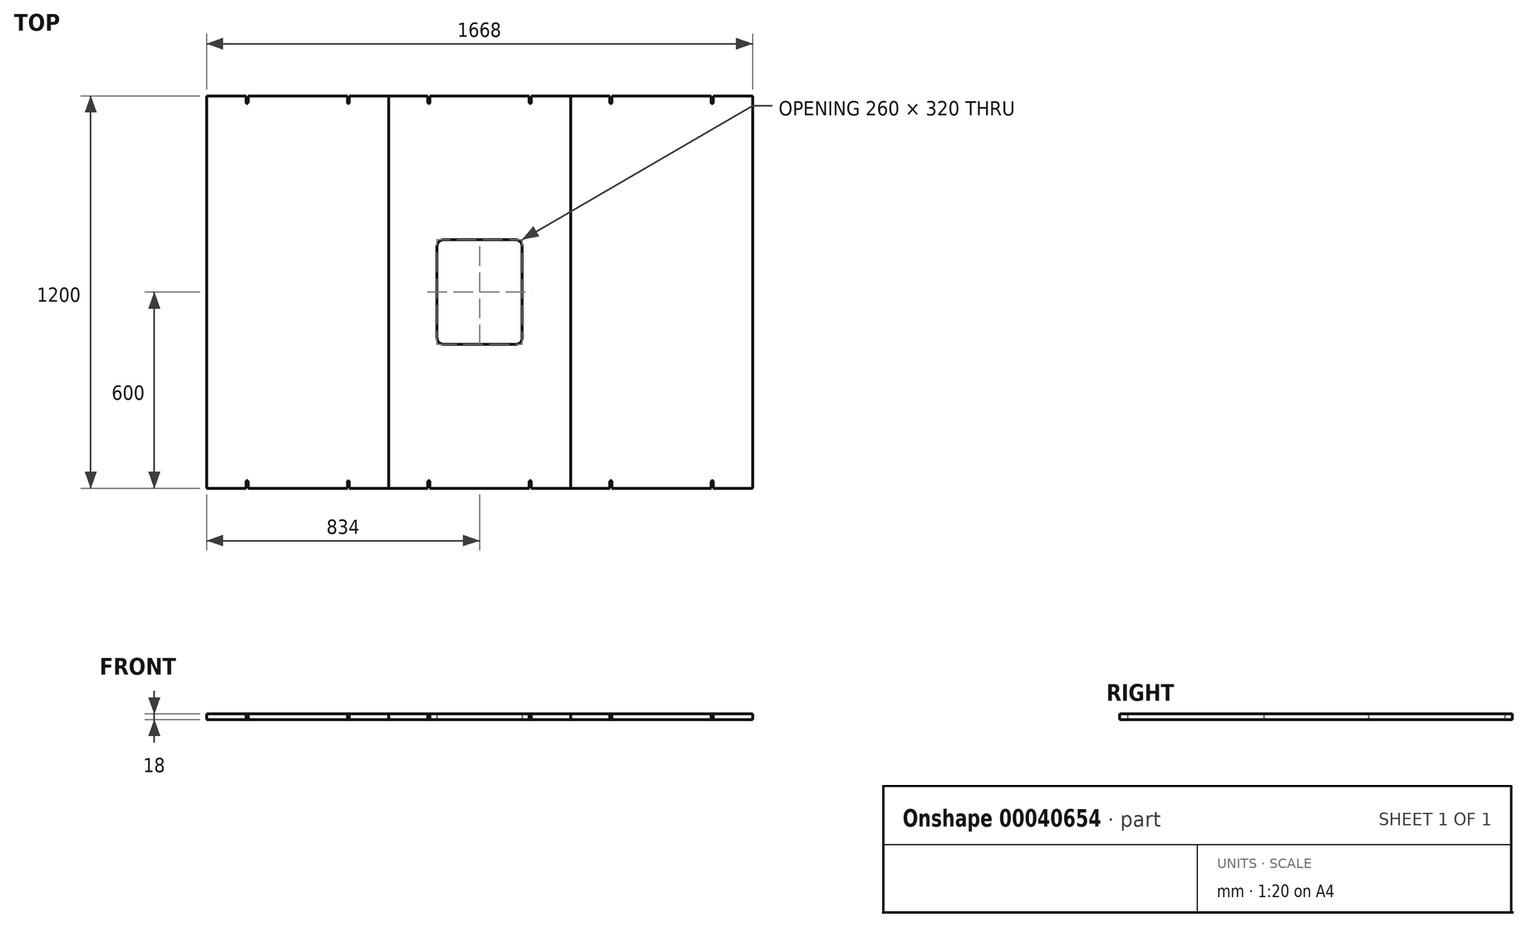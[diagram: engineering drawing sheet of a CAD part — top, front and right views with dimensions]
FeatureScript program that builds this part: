
annotation { "Feature Type Name" : "Feature", "Feature Type Description" : "" }
export const myFeature = defineFeature(function(context is Context, id is Id, definition is map)
    precondition{}
    {
        {
            var Q0;
            Q0=qCreatedBy(makeId("Top.planeOp"),FACE);
            var sketch = newSketch(context, id + "F0", { "sketchPlane" : qUnion([Q0])});
            skLineSegment(sketch, "E0.left", {"start": v(834, 600) * mm, "end": v(834, -600) * mm});
            skLineSegment(sketch, "E0.right", {"start": v(-834, 600) * mm, "end": v(-834, -600) * mm});
            skPoint(sketch, "E0.middle", {"position": v(0, 0) * mm});
            skLineSegment(sketch, "E1.bottom", {"start": v(130, 160) * mm, "end": v(-130, 160) * mm});
            skLineSegment(sketch, "E1.top", {"start": v(130, -160) * mm, "end": v(-130, -160) * mm});
            skLineSegment(sketch, "E1.left", {"start": v(130, 160) * mm, "end": v(130, -160) * mm});
            skLineSegment(sketch, "E1.right", {"start": v(-130, 160) * mm, "end": v(-130, -160) * mm});
            skLineSegment(sketch, "E2", {"start": v(-278, 600) * mm, "end": v(-278, -600) * mm});
            skLineSegment(sketch, "E3", {"start": v(278, 600) * mm, "end": v(278, -600) * mm});
            skLineSegment(sketch, "E4", {"start": v(-834, 600) * mm, "end": v(-278, 600) * mm});
            skLineSegment(sketch, "E5", {"start": v(-278, 600) * mm, "end": v(278, 600) * mm});
            skLineSegment(sketch, "E6", {"start": v(278, 600) * mm, "end": v(834, 600) * mm});
            skLineSegment(sketch, "E7", {"start": v(-834, -600) * mm, "end": v(-278, -600) * mm});
            skLineSegment(sketch, "E8", {"start": v(-278, -600) * mm, "end": v(278, -600) * mm});
            skLineSegment(sketch, "E9", {"start": v(278, -600) * mm, "end": v(834, -600) * mm});
            skArc(sketch, "E10", {"start": v(-714, 580) * mm, "mid": v(-710.9, 576.9) * mm, "end": v(-707.8, 580) * mm});
            skLineSegment(sketch, "E11.top", {"start": v(-714, 600) * mm, "end": v(-707.8, 600) * mm});
            skLineSegment(sketch, "E11.left", {"start": v(-714, 580) * mm, "end": v(-714, 600) * mm});
            skLineSegment(sketch, "E11.right", {"start": v(-707.8, 580) * mm, "end": v(-707.8, 600) * mm});
            skLineSegment(sketch, "E12", {"start": v(-556, 600) * mm, "end": v(-556, 638.6) * mm, "construction": true});
            skLineSegment(sketch, "E13.MirrorCS", {"start": v(-404.2, 580) * mm, "end": v(-404.2, 600) * mm});
            skArc(sketch, "E14.MirrorCS", {"start": v(-398, 580) * mm, "mid": v(-401.1, 576.9) * mm, "end": v(-404.2, 580) * mm});
            skLineSegment(sketch, "E15.MirrorCS", {"start": v(-398, 580) * mm, "end": v(-398, 600) * mm});
            skLineSegment(sketch, "E16.1.0.0", {"start": v(-158, 580) * mm, "end": v(-158, 600) * mm});
            skArc(sketch, "E16.1.0.1", {"start": v(-158, 580) * mm, "mid": v(-154.9, 576.9) * mm, "end": v(-151.8, 580) * mm});
            skLineSegment(sketch, "E16.1.0.2", {"start": v(-151.8, 580) * mm, "end": v(-151.8, 600) * mm});
            skLineSegment(sketch, "E16.1.0.3", {"start": v(151.8, 580) * mm, "end": v(151.8, 600) * mm});
            skArc(sketch, "E16.1.0.4", {"start": v(158, 580) * mm, "mid": v(154.9, 576.9) * mm, "end": v(151.8, 580) * mm});
            skLineSegment(sketch, "E16.1.0.5", {"start": v(158, 580) * mm, "end": v(158, 600) * mm});
            skLineSegment(sketch, "E16.2.0.0", {"start": v(398, 580) * mm, "end": v(398, 600) * mm});
            skArc(sketch, "E16.2.0.1", {"start": v(398, 580) * mm, "mid": v(401.1, 576.9) * mm, "end": v(404.2, 580) * mm});
            skLineSegment(sketch, "E16.2.0.2", {"start": v(404.2, 580) * mm, "end": v(404.2, 600) * mm});
            skLineSegment(sketch, "E16.2.0.3", {"start": v(707.8, 580) * mm, "end": v(707.8, 600) * mm});
            skArc(sketch, "E16.2.0.4", {"start": v(714, 580) * mm, "mid": v(710.9, 576.9) * mm, "end": v(707.8, 580) * mm});
            skLineSegment(sketch, "E16.2.0.5", {"start": v(714, 580) * mm, "end": v(714, 600) * mm});
            skLineSegment(sketch, "E16.direction1", {"start": v(-714, 580) * mm, "end": v(-158, 580) * mm, "construction": true});
            skLineSegment(sketch, "E17.MirrorCS", {"start": v(-714, -580) * mm, "end": v(-714, -600) * mm});
            skArc(sketch, "E18.MirrorCS", {"start": v(-714, -580) * mm, "mid": v(-710.9, -576.9) * mm, "end": v(-707.8, -580) * mm});
            skLineSegment(sketch, "E19.MirrorCS", {"start": v(-707.8, -580) * mm, "end": v(-707.8, -600) * mm});
            skLineSegment(sketch, "E20.MirrorCS", {"start": v(-404.2, -580) * mm, "end": v(-404.2, -600) * mm});
            skArc(sketch, "E21.MirrorCS", {"start": v(-398, -580) * mm, "mid": v(-401.1, -576.9) * mm, "end": v(-404.2, -580) * mm});
            skLineSegment(sketch, "E22.MirrorCS", {"start": v(-398, -580) * mm, "end": v(-398, -600) * mm});
            skLineSegment(sketch, "E23.MirrorCS", {"start": v(-158, -580) * mm, "end": v(-158, -600) * mm});
            skArc(sketch, "E24.MirrorCS", {"start": v(-158, -580) * mm, "mid": v(-154.9, -576.9) * mm, "end": v(-151.8, -580) * mm});
            skLineSegment(sketch, "E25.MirrorCS", {"start": v(-151.8, -580) * mm, "end": v(-151.8, -600) * mm});
            skLineSegment(sketch, "E26.MirrorCS", {"start": v(151.8, -580) * mm, "end": v(151.8, -600) * mm});
            skArc(sketch, "E27.MirrorCS", {"start": v(158, -580) * mm, "mid": v(154.9, -576.9) * mm, "end": v(151.8, -580) * mm});
            skLineSegment(sketch, "E28.MirrorCS", {"start": v(158, -580) * mm, "end": v(158, -600) * mm});
            skLineSegment(sketch, "E29.MirrorCS", {"start": v(398, -580) * mm, "end": v(398, -600) * mm});
            skArc(sketch, "E30.MirrorCS", {"start": v(398, -580) * mm, "mid": v(401.1, -576.9) * mm, "end": v(404.2, -580) * mm});
            skLineSegment(sketch, "E31.MirrorCS", {"start": v(404.2, -580) * mm, "end": v(404.2, -600) * mm});
            skLineSegment(sketch, "E32.MirrorCS", {"start": v(707.8, -580) * mm, "end": v(707.8, -600) * mm});
            skArc(sketch, "E33.MirrorCS", {"start": v(714, -580) * mm, "mid": v(710.9, -576.9) * mm, "end": v(707.8, -580) * mm});
            skLineSegment(sketch, "E34.MirrorCS", {"start": v(714, -580) * mm, "end": v(714, -600) * mm});
            skSolve(sketch);
        }
        {
            var Q0;
            Q0=makeQuery(id+"F0.imprint","IMPRINT",FACE,{"disambiguationData":[TD([[makeQuery(id+"F0.imprint","IMPRINT",EDGE,{"derivedFrom":sQuery(id+"F0.wireOp",EDGE,"E1.bottom")}),-1.0]])]});
            extrude(context, id + "F1", {"entities" : qUnion([Q0]), "flatOperationType" : FlatOperationType.REMOVE, "depth" : 18 * mm, "offsetDistance" : 25 * mm, "domain" : OperationDomain.MODEL});
        }
        {
            var Q0;
            {var subQ5=sQuery(id+"F0.wireOp",EDGE,"E0.right");Q0=makeQuery(id+"F0.imprint","IMPRINT",FACE,{"disambiguationData":[TD([[makeQuery(id+"F0.imprint","IMPRINT",EDGE,{"derivedFrom":subQ5}),1.0]])]});}
            var Q1;
            Q1=makeQuery(id+"F1.opExtrude","CAP_FACE",FACE,{"disambiguationData":[OSD([sQuery(id+"F0.wireOp",EDGE,"E1.bottom"),sQuery(id+"F0.wireOp",EDGE,"E1.top"),sQuery(id+"F0.wireOp",EDGE,"E1.left"),sQuery(id+"F0.wireOp",EDGE,"E1.right"),sQuery(id+"F0.wireOp",EDGE,"E2"),sQuery(id+"F0.wireOp",EDGE,"E3"),sQuery(id+"F0.wireOp",EDGE,"E5"),sQuery(id+"F0.wireOp",EDGE,"E8"),sQuery(id+"F0.wireOp",EDGE,"E16.1.0.0"),sQuery(id+"F0.wireOp",EDGE,"E16.1.0.1"),sQuery(id+"F0.wireOp",EDGE,"E16.1.0.2"),sQuery(id+"F0.wireOp",EDGE,"E16.1.0.3"),sQuery(id+"F0.wireOp",EDGE,"E16.1.0.4"),sQuery(id+"F0.wireOp",EDGE,"E16.1.0.5"),sQuery(id+"F0.wireOp",EDGE,"E23.MirrorCS"),sQuery(id+"F0.wireOp",EDGE,"E24.MirrorCS"),sQuery(id+"F0.wireOp",EDGE,"E25.MirrorCS"),sQuery(id+"F0.wireOp",EDGE,"E26.MirrorCS"),sQuery(id+"F0.wireOp",EDGE,"E27.MirrorCS"),sQuery(id+"F0.wireOp",EDGE,"E28.MirrorCS")])],"isStart":false});
            extrude(context, id + "F2", {"entities" : qUnion([Q0]), "endBound" : BoundingType.UP_TO_SURFACE, "depth" : 18 * mm, "endBoundEntityFace" : qUnion([Q1]), "offsetDistance" : 25 * mm});
        }
        {
            var Q0;
            {var subQ1=sQuery(id+"F0.wireOp",EDGE,"E0.left");Q0=makeQuery(id+"F0.imprint","IMPRINT",FACE,{"disambiguationData":[TD([[makeQuery(id+"F0.imprint","IMPRINT",EDGE,{"derivedFrom":subQ1}),-1.0]])]});}
            var Q1;
            Q1=makeQuery(id+"F1.opExtrude","CAP_FACE",FACE,{"disambiguationData":[OSD([sQuery(id+"F0.wireOp",EDGE,"E1.bottom"),sQuery(id+"F0.wireOp",EDGE,"E1.top"),sQuery(id+"F0.wireOp",EDGE,"E1.left"),sQuery(id+"F0.wireOp",EDGE,"E1.right"),sQuery(id+"F0.wireOp",EDGE,"E2"),sQuery(id+"F0.wireOp",EDGE,"E3"),sQuery(id+"F0.wireOp",EDGE,"E5"),sQuery(id+"F0.wireOp",EDGE,"E8"),sQuery(id+"F0.wireOp",EDGE,"E16.1.0.0"),sQuery(id+"F0.wireOp",EDGE,"E16.1.0.1"),sQuery(id+"F0.wireOp",EDGE,"E16.1.0.2"),sQuery(id+"F0.wireOp",EDGE,"E16.1.0.3"),sQuery(id+"F0.wireOp",EDGE,"E16.1.0.4"),sQuery(id+"F0.wireOp",EDGE,"E16.1.0.5"),sQuery(id+"F0.wireOp",EDGE,"E23.MirrorCS"),sQuery(id+"F0.wireOp",EDGE,"E24.MirrorCS"),sQuery(id+"F0.wireOp",EDGE,"E25.MirrorCS"),sQuery(id+"F0.wireOp",EDGE,"E26.MirrorCS"),sQuery(id+"F0.wireOp",EDGE,"E27.MirrorCS"),sQuery(id+"F0.wireOp",EDGE,"E28.MirrorCS")])],"isStart":false});
            extrude(context, id + "F3", {"entities" : qUnion([Q0]), "endBound" : BoundingType.UP_TO_SURFACE, "depth" : 25 * mm, "endBoundEntityFace" : qUnion([Q1]), "offsetDistance" : 25 * mm});
        }
        {
            var Q0;
            Q0=makeQuery(id+"F1.opExtrude","SWEPT_EDGE",EDGE,{"disambiguationData":[OSD([sQuery(id+"F0.wireOp",EDGE,"E1.bottom"),sQuery(id+"F0.wireOp",EDGE,"E1.right")])]});
            var Q1;
            Q1=makeQuery(id+"F1.opExtrude","SWEPT_EDGE",EDGE,{"disambiguationData":[OSD([sQuery(id+"F0.wireOp",EDGE,"E1.bottom"),sQuery(id+"F0.wireOp",EDGE,"E1.left")])]});
            var Q2;
            Q2=makeQuery(id+"F1.opExtrude","SWEPT_EDGE",EDGE,{"disambiguationData":[OSD([sQuery(id+"F0.wireOp",EDGE,"E1.top"),sQuery(id+"F0.wireOp",EDGE,"E1.right")])]});
            var Q3;
            Q3=makeQuery(id+"F1.opExtrude","SWEPT_EDGE",EDGE,{"disambiguationData":[OSD([sQuery(id+"F0.wireOp",EDGE,"E1.top"),sQuery(id+"F0.wireOp",EDGE,"E1.left")])]});
            fillet(context, id + "F4", {"entities" : qUnion([Q0, Q1, Q2, Q3]), "tangentPropagation" : true, "radius" : 20 * mm, "defaultsChanged" : true, "vertexSettings" : [], "allowEdgeOverflow" : false});
        }
    });
